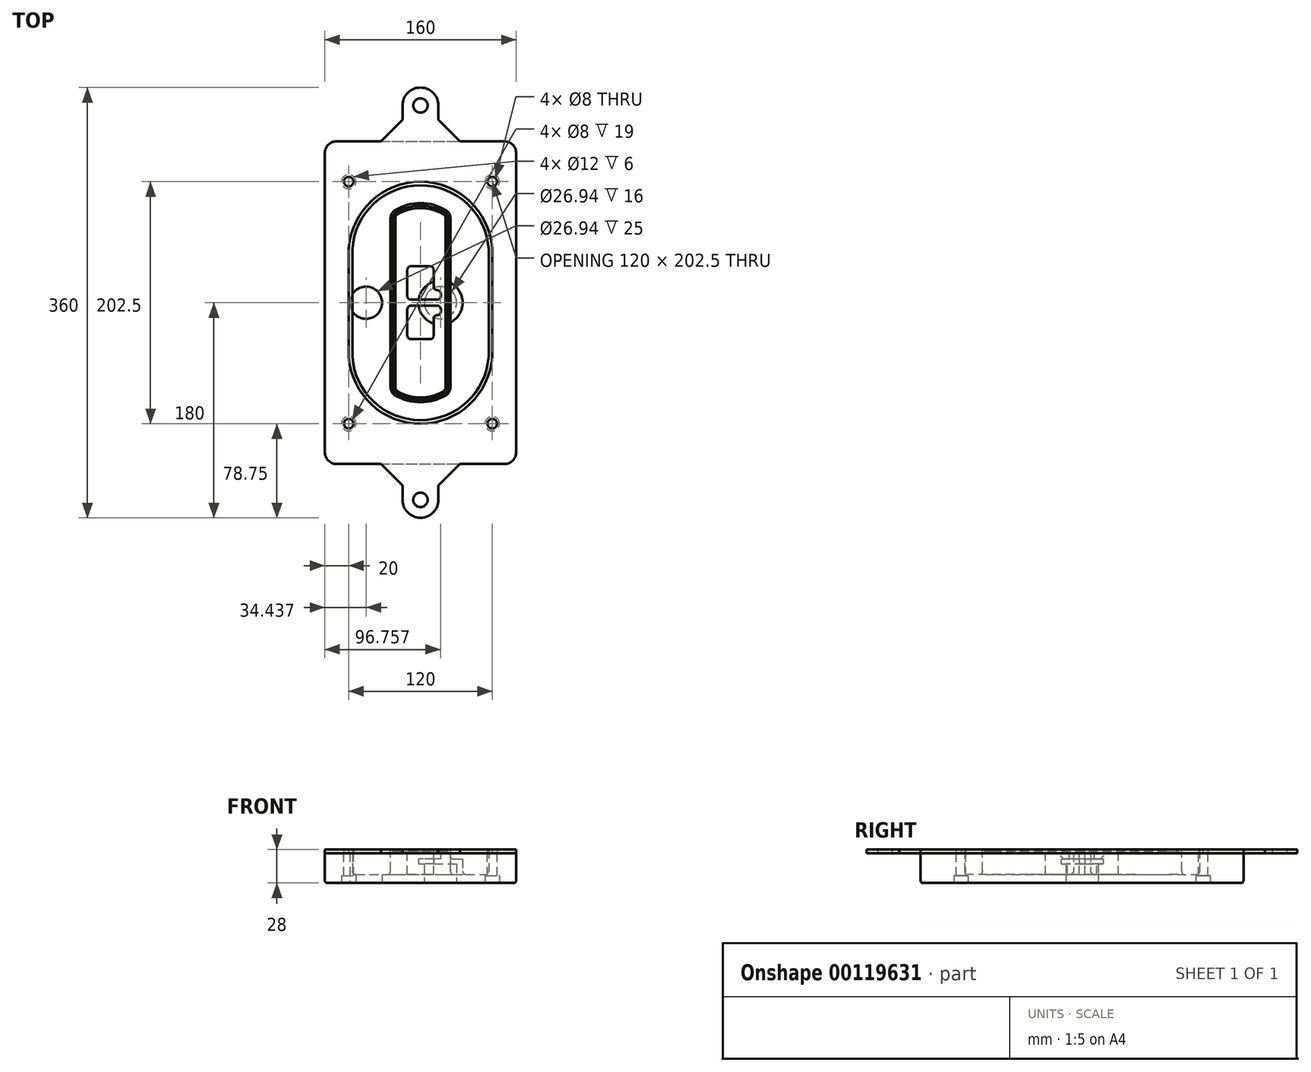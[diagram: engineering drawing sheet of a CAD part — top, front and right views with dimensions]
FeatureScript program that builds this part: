
annotation { "Feature Type Name" : "Feature", "Feature Type Description" : "" }
export const myFeature = defineFeature(function(context is Context, id is Id, definition is map)
    precondition{}
    {
        {
            var Q0;
            Q0=qCreatedBy(makeId("Top.planeOp"),FACE);
            var sketch = newSketch(context, id + "F0", { "sketchPlane" : qUnion([Q0])});
            skPoint(sketch, "E0.rect.middle", {"position": v(0, 0) * mm});
            skLineSegment(sketch, "E1.bottom", {"start": v(-70, -135) * mm, "end": v(70, -135) * mm});
            skLineSegment(sketch, "E1.top", {"start": v(-70, 135) * mm, "end": v(70, 135) * mm});
            skLineSegment(sketch, "E1.left", {"start": v(-80, -125) * mm, "end": v(-80, 125) * mm});
            skLineSegment(sketch, "E1.right", {"start": v(80, -125) * mm, "end": v(80, 125) * mm});
            skLineSegment(sketch, "E2", {"start": v(-80, 135) * mm, "end": v(80, -135) * mm, "construction": true});
            skLineSegment(sketch, "E3", {"start": v(80, 135) * mm, "end": v(-80, -135) * mm, "construction": true});
            skCircle(sketch, "E4", {"center": v(-60, 101.25) * mm, "radius": 4 * mm});
            skCircle(sketch, "E5", {"center": v(60, 101.25) * mm, "radius": 4 * mm});
            skCircle(sketch, "E6", {"center": v(60, -101.25) * mm, "radius": 4 * mm});
            skCircle(sketch, "E7", {"center": v(-60, -101.25) * mm, "radius": 4 * mm});
            skLineSegment(sketch, "E8", {"start": v(-60, 101.25) * mm, "end": v(60, 101.25) * mm, "construction": true});
            skLineSegment(sketch, "E9", {"start": v(60, 101.25) * mm, "end": v(60, -101.25) * mm, "construction": true});
            skLineSegment(sketch, "E10", {"start": v(60, -101.25) * mm, "end": v(-60, -101.25) * mm, "construction": true});
            skLineSegment(sketch, "E11", {"start": v(-60, -101.25) * mm, "end": v(-60, 101.25) * mm, "construction": true});
            skLineSegment(sketch, "E12", {"start": v(-60, 44.66) * mm, "end": v(-60, -44.66) * mm});
            skLineSegment(sketch, "E13", {"start": v(60, 44.66) * mm, "end": v(60, -44.66) * mm});
            skArc(sketch, "E14", {"start": v(59.98, 45.37) * mm, "mid": v(0, 101.25) * mm, "end": v(-59.98, 45.37) * mm});
            skArc(sketch, "E15", {"start": v(-59.98, -45.37) * mm, "mid": v(0, -101.25) * mm, "end": v(59.98, -45.37) * mm});
            skLineSegment(sketch, "E16", {"start": v(-60, 0) * mm, "end": v(60, 0) * mm, "construction": true});
            skPoint(sketch, "E17.visualSharp", {"position": v(-60, -45) * mm});
            skArc(sketch, "E17.filletArc", {"start": v(-60, -44.66) * mm, "mid": v(-60, -45.02) * mm, "end": v(-59.98, -45.37) * mm});
            skPoint(sketch, "E18.visualSharp", {"position": v(-60, 45) * mm});
            skArc(sketch, "E18.filletArc", {"start": v(-59.98, 45.37) * mm, "mid": v(-60, 45.02) * mm, "end": v(-60, 44.66) * mm});
            skPoint(sketch, "E19.visualSharp", {"position": v(60, 45) * mm});
            skArc(sketch, "E19.filletArc", {"start": v(60, 44.66) * mm, "mid": v(60, 45.02) * mm, "end": v(59.98, 45.37) * mm});
            skPoint(sketch, "E20.visualSharp", {"position": v(60, -45) * mm});
            skArc(sketch, "E20.filletArc", {"start": v(59.98, -45.37) * mm, "mid": v(60, -45.02) * mm, "end": v(60, -44.66) * mm});
            skPoint(sketch, "E21.visualSharp", {"position": v(-80, 135) * mm});
            skArc(sketch, "E21.filletArc", {"start": v(-70, 135) * mm, "mid": v(-77.07, 132.07) * mm, "end": v(-80, 125) * mm});
            skPoint(sketch, "E22.visualSharp", {"position": v(80, 135) * mm});
            skArc(sketch, "E22.filletArc", {"start": v(80, 125) * mm, "mid": v(77.07, 132.07) * mm, "end": v(70, 135) * mm});
            skPoint(sketch, "E23.visualSharp", {"position": v(80, -135) * mm});
            skArc(sketch, "E23.filletArc", {"start": v(70, -135) * mm, "mid": v(77.07, -132.07) * mm, "end": v(80, -125) * mm});
            skPoint(sketch, "E24.visualSharp", {"position": v(-80, -135) * mm});
            skArc(sketch, "E24.filletArc", {"start": v(-80, -125) * mm, "mid": v(-77.07, -132.07) * mm, "end": v(-70, -135) * mm});
            skArc(sketch, "E25.0", {"start": v(57, 44.66) * mm, "mid": v(57, 44.9) * mm, "end": v(56.98, 45.16) * mm});
            skLineSegment(sketch, "E25.1", {"start": v(57, 44.66) * mm, "end": v(57, -44.66) * mm});
            skArc(sketch, "E25.2", {"start": v(56.98, -45.16) * mm, "mid": v(57, -44.9) * mm, "end": v(57, -44.66) * mm});
            skArc(sketch, "E25.3", {"start": v(-56.98, -45.16) * mm, "mid": v(0, -98.25) * mm, "end": v(56.98, -45.16) * mm});
            skArc(sketch, "E25.4", {"start": v(-57, -44.66) * mm, "mid": v(-57, -44.9) * mm, "end": v(-56.98, -45.16) * mm});
            skArc(sketch, "E25.5", {"start": v(56.98, 45.16) * mm, "mid": v(0, 98.25) * mm, "end": v(-56.98, 45.16) * mm});
            skLineSegment(sketch, "E25.6", {"start": v(-57, 44.66) * mm, "end": v(-57, -44.66) * mm});
            skArc(sketch, "E25.7", {"start": v(-56.98, 45.16) * mm, "mid": v(-57, 44.9) * mm, "end": v(-57, 44.66) * mm});
            skArc(sketch, "E26.0", {"start": v(-63.97, 45.65) * mm, "mid": v(-64, 45.16) * mm, "end": v(-64, 44.66) * mm});
            skArc(sketch, "E26.1", {"start": v(63.97, 45.65) * mm, "mid": v(0, 105.25) * mm, "end": v(-63.97, 45.65) * mm});
            skArc(sketch, "E26.2", {"start": v(64, 44.66) * mm, "mid": v(64, 45.16) * mm, "end": v(63.97, 45.65) * mm});
            skLineSegment(sketch, "E26.3", {"start": v(64, 44.66) * mm, "end": v(64, -44.66) * mm});
            skArc(sketch, "E26.4", {"start": v(63.97, -45.65) * mm, "mid": v(64, -45.16) * mm, "end": v(64, -44.66) * mm});
            skLineSegment(sketch, "E26.5", {"start": v(-64, 44.66) * mm, "end": v(-64, -44.66) * mm});
            skArc(sketch, "E26.6", {"start": v(-63.97, -45.65) * mm, "mid": v(0, -105.25) * mm, "end": v(63.97, -45.65) * mm});
            skArc(sketch, "E26.7", {"start": v(-64, -44.66) * mm, "mid": v(-64, -45.16) * mm, "end": v(-63.97, -45.65) * mm});
            skSolve(sketch);
        }
        {
            var Q0;
            Q0=makeQuery(id+"F0.imprint","IMPRINT",FACE,{"disambiguationData":[TD([[makeQuery(id+"F0.imprint","IMPRINT",EDGE,{"derivedFrom":sQuery(id+"F0.wireOp",EDGE,"E1.bottom")}),1.0]])]});
            var Q1;
            Q1=makeQuery(id+"F0.imprint","IMPRINT",FACE,{"disambiguationData":[TD([[makeQuery(id+"F0.imprint","IMPRINT",EDGE,{"derivedFrom":sQuery(id+"F0.wireOp",EDGE,"E12")}),1.0]])]});
            var Q2;
            Q2=makeQuery(id+"F0.imprint","IMPRINT",FACE,{"disambiguationData":[TD([[makeQuery(id+"F0.imprint","IMPRINT",EDGE,{"derivedFrom":sQuery(id+"F0.wireOp",EDGE,"E25.0")}),1.0]])]});
            var Q3;
            Q3=makeQuery(id+"F0.imprint","IMPRINT",FACE,{"disambiguationData":[TD([[makeQuery(id+"F0.imprint","IMPRINT",EDGE,{"derivedFrom":sQuery(id+"F0.wireOp",EDGE,"E12")}),-1.0]])]});
            extrude(context, id + "F1", {"entities" : qUnion([Q0, Q1, Q2, Q3]), "oppositeDirection" : true, "depth" : 25 * mm});
        }
        {
            var Q0;
            Q0=makeQuery(id+"F0.imprint","IMPRINT",FACE,{"disambiguationData":[TD([[makeQuery(id+"F0.imprint","IMPRINT",EDGE,{"derivedFrom":sQuery(id+"F0.wireOp",EDGE,"E12")}),1.0]])]});
            extrude(context, id + "F2", {"entities" : qUnion([Q0]), "operationType" : NewBodyOperationType.ADD, "depth" : 3 * mm});
        }
        {
            var Q0;
            Q0=makeQuery(id+"F0.imprint","IMPRINT",FACE,{"disambiguationData":[TD([[makeQuery(id+"F0.imprint","IMPRINT",EDGE,{"derivedFrom":sQuery(id+"F0.wireOp",EDGE,"E25.0")}),1.0]])]});
            extrude(context, id + "F3", {"entities" : qUnion([Q0]), "operationType" : NewBodyOperationType.REMOVE, "oppositeDirection" : true, "depth" : 18 * mm});
        }
        {
            var Q0;
            Q0=makeQuery(id+"F2.opExtrude","CAP_FACE",FACE,{"disambiguationData":[OSD([sQuery(id+"F0.wireOp",EDGE,"E12"),sQuery(id+"F0.wireOp",EDGE,"E13"),sQuery(id+"F0.wireOp",EDGE,"E14"),sQuery(id+"F0.wireOp",EDGE,"E15"),sQuery(id+"F0.wireOp",EDGE,"E17.filletArc"),sQuery(id+"F0.wireOp",EDGE,"E18.filletArc"),sQuery(id+"F0.wireOp",EDGE,"E19.filletArc"),sQuery(id+"F0.wireOp",EDGE,"E20.filletArc"),sQuery(id+"F0.wireOp",EDGE,"E25.0"),sQuery(id+"F0.wireOp",EDGE,"E25.1"),sQuery(id+"F0.wireOp",EDGE,"E25.2"),sQuery(id+"F0.wireOp",EDGE,"E25.3"),sQuery(id+"F0.wireOp",EDGE,"E25.4"),sQuery(id+"F0.wireOp",EDGE,"E25.5"),sQuery(id+"F0.wireOp",EDGE,"E25.6"),sQuery(id+"F0.wireOp",EDGE,"E25.7")])],"isStart":false});
            var sketch = newSketch(context, id + "F4", { "sketchPlane" : qUnion([Q0])});
            skArc(sketch, "E27.0", {"start": v(-20.99, -77.65) * mm, "mid": v(0, -83.25) * mm, "end": v(20.99, -77.65) * mm});
            skArc(sketch, "E28.0", {"start": v(20.99, 77.65) * mm, "mid": v(0, 83.25) * mm, "end": v(-20.99, 77.65) * mm});
            skLineSegment(sketch, "E29", {"start": v(-25, 70.71) * mm, "end": v(-25, -70.71) * mm});
            skLineSegment(sketch, "E30", {"start": v(25, 70.71) * mm, "end": v(25, -70.71) * mm});
            skLineSegment(sketch, "E31", {"start": v(-25, 75.03) * mm, "end": v(25, 75.03) * mm, "construction": true});
            skLineSegment(sketch, "E32", {"start": v(-25, -75.03) * mm, "end": v(25, -75.03) * mm, "construction": true});
            skPoint(sketch, "E33.visualSharp", {"position": v(-25, 75.03) * mm});
            skArc(sketch, "E33.filletArc", {"start": v(-20.99, 77.65) * mm, "mid": v(-23.92, 74.72) * mm, "end": v(-25, 70.71) * mm});
            skPoint(sketch, "E34.visualSharp", {"position": v(25, 75.03) * mm});
            skArc(sketch, "E34.filletArc", {"start": v(25, 70.71) * mm, "mid": v(23.92, 74.72) * mm, "end": v(20.99, 77.65) * mm});
            skPoint(sketch, "E35.visualSharp", {"position": v(25, -75.03) * mm});
            skArc(sketch, "E35.filletArc", {"start": v(20.99, -77.65) * mm, "mid": v(23.92, -74.72) * mm, "end": v(25, -70.71) * mm});
            skPoint(sketch, "E36.visualSharp", {"position": v(-25, -75.03) * mm});
            skArc(sketch, "E36.filletArc", {"start": v(-25, -70.71) * mm, "mid": v(-23.92, -74.72) * mm, "end": v(-20.99, -77.65) * mm});
            skArc(sketch, "E37.0", {"start": v(56.98, 45.16) * mm, "mid": v(0, 98.25) * mm, "end": v(-56.98, 45.16) * mm});
            skArc(sketch, "E37.1", {"start": v(-56.98, 45.16) * mm, "mid": v(-57, 44.9) * mm, "end": v(-57, 44.66) * mm});
            skLineSegment(sketch, "E37.2", {"start": v(-57, 44.66) * mm, "end": v(-57, -44.66) * mm});
            skArc(sketch, "E37.3", {"start": v(-57, -44.66) * mm, "mid": v(-57, -44.9) * mm, "end": v(-56.98, -45.16) * mm});
            skArc(sketch, "E37.4", {"start": v(-56.98, -45.16) * mm, "mid": v(0, -98.25) * mm, "end": v(56.98, -45.16) * mm});
            skArc(sketch, "E37.5", {"start": v(56.98, -45.16) * mm, "mid": v(57, -44.9) * mm, "end": v(57, -44.66) * mm});
            skLineSegment(sketch, "E37.6", {"start": v(57, 44.66) * mm, "end": v(57, -44.66) * mm});
            skArc(sketch, "E37.7", {"start": v(57, 44.66) * mm, "mid": v(57, 44.9) * mm, "end": v(56.98, 45.16) * mm});
            skLineSegment(sketch, "E38.0", {"start": v(23, 70.71) * mm, "end": v(23, -70.71) * mm});
            skArc(sketch, "E38.1", {"start": v(19.99, -75.92) * mm, "mid": v(22.2, -73.72) * mm, "end": v(23, -70.71) * mm});
            skArc(sketch, "E38.2", {"start": v(-19.99, -75.92) * mm, "mid": v(0, -81.25) * mm, "end": v(19.99, -75.92) * mm});
            skArc(sketch, "E38.3", {"start": v(-23, -70.71) * mm, "mid": v(-22.2, -73.72) * mm, "end": v(-19.99, -75.92) * mm});
            skLineSegment(sketch, "E38.4", {"start": v(-23, 70.71) * mm, "end": v(-23, -70.71) * mm});
            skArc(sketch, "E38.5", {"start": v(23, 70.71) * mm, "mid": v(22.2, 73.72) * mm, "end": v(19.99, 75.92) * mm});
            skArc(sketch, "E38.6", {"start": v(-19.99, 75.92) * mm, "mid": v(-22.2, 73.72) * mm, "end": v(-23, 70.71) * mm});
            skArc(sketch, "E38.7", {"start": v(19.99, 75.92) * mm, "mid": v(0, 81.25) * mm, "end": v(-19.99, 75.92) * mm});
            skArc(sketch, "E39.0", {"start": v(21, 70.71) * mm, "mid": v(20.46, 72.72) * mm, "end": v(19, 74.18) * mm});
            skLineSegment(sketch, "E39.1", {"start": v(21, 70.71) * mm, "end": v(21, -70.71) * mm});
            skArc(sketch, "E39.2", {"start": v(19, -74.18) * mm, "mid": v(20.46, -72.72) * mm, "end": v(21, -70.71) * mm});
            skArc(sketch, "E39.3", {"start": v(-19, -74.18) * mm, "mid": v(0, -79.25) * mm, "end": v(19, -74.18) * mm});
            skArc(sketch, "E39.4", {"start": v(-21, -70.71) * mm, "mid": v(-20.46, -72.72) * mm, "end": v(-19, -74.18) * mm});
            skArc(sketch, "E39.5", {"start": v(19, 74.18) * mm, "mid": v(0, 79.25) * mm, "end": v(-19, 74.18) * mm});
            skLineSegment(sketch, "E39.6", {"start": v(-21, 70.71) * mm, "end": v(-21, -70.71) * mm});
            skArc(sketch, "E39.7", {"start": v(-19, 74.18) * mm, "mid": v(-20.46, 72.72) * mm, "end": v(-21, 70.71) * mm});
            skLineSegment(sketch, "E40", {"start": v(-25, 0) * mm, "end": v(25, 0) * mm, "construction": true});
            skLineSegment(sketch, "E41", {"start": v(-11, 5.5) * mm, "end": v(-11, 27.5) * mm});
            skLineSegment(sketch, "E42", {"start": v(-8, 30.5) * mm, "end": v(8, 30.5) * mm});
            skLineSegment(sketch, "E43", {"start": v(11, 27.5) * mm, "end": v(11, 13.5) * mm});
            skLineSegment(sketch, "E44", {"start": v(14, 10.5) * mm, "end": v(14, 10.5) * mm});
            skLineSegment(sketch, "E45", {"start": v(17, 7.5) * mm, "end": v(17, 5.5) * mm});
            skLineSegment(sketch, "E46", {"start": v(14, 2.5) * mm, "end": v(-8, 2.5) * mm});
            skPoint(sketch, "E47.visualSharp", {"position": v(-11, 30.5) * mm});
            skArc(sketch, "E47.filletArc", {"start": v(-8, 30.5) * mm, "mid": v(-10.12, 29.62) * mm, "end": v(-11, 27.5) * mm});
            skPoint(sketch, "E48.visualSharp", {"position": v(11, 30.5) * mm});
            skArc(sketch, "E48.filletArc", {"start": v(11, 27.5) * mm, "mid": v(10.12, 29.62) * mm, "end": v(8, 30.5) * mm});
            skPoint(sketch, "E49.visualSharp", {"position": v(11, 10.5) * mm});
            skArc(sketch, "E49.filletArc", {"start": v(11, 13.5) * mm, "mid": v(11.88, 11.38) * mm, "end": v(14, 10.5) * mm});
            skPoint(sketch, "E50.visualSharp", {"position": v(17, 10.5) * mm});
            skArc(sketch, "E50.filletArc", {"start": v(17, 7.5) * mm, "mid": v(16.12, 9.62) * mm, "end": v(14, 10.5) * mm});
            skPoint(sketch, "E51.visualSharp", {"position": v(17, 2.5) * mm});
            skArc(sketch, "E51.filletArc", {"start": v(14, 2.5) * mm, "mid": v(16.12, 3.38) * mm, "end": v(17, 5.5) * mm});
            skPoint(sketch, "E52.visualSharp", {"position": v(-11, 2.5) * mm});
            skArc(sketch, "E52.filletArc", {"start": v(-11, 5.5) * mm, "mid": v(-10.12, 3.38) * mm, "end": v(-8, 2.5) * mm});
            skLineSegment(sketch, "E53.0.MirrorCS", {"start": v(14, -2.5) * mm, "end": v(-8, -2.5) * mm});
            skArc(sketch, "E54.0.MirrorCS", {"start": v(-11, -5.5) * mm, "mid": v(-10.12, -3.38) * mm, "end": v(-8, -2.5) * mm});
            skLineSegment(sketch, "E55.0.MirrorCS", {"start": v(-11, -5.5) * mm, "end": v(-11, -27.5) * mm});
            skArc(sketch, "E56.0.MirrorCS", {"start": v(-8, -30.5) * mm, "mid": v(-10.12, -29.62) * mm, "end": v(-11, -27.5) * mm});
            skLineSegment(sketch, "E57.0.MirrorCS", {"start": v(-8, -30.5) * mm, "end": v(8, -30.5) * mm});
            skArc(sketch, "E58.0.MirrorCS", {"start": v(11, -27.5) * mm, "mid": v(10.12, -29.62) * mm, "end": v(8, -30.5) * mm});
            skLineSegment(sketch, "E59.0.MirrorCS", {"start": v(11, -27.5) * mm, "end": v(11, -13.5) * mm});
            skArc(sketch, "E60.0.MirrorCS", {"start": v(11, -13.5) * mm, "mid": v(11.88, -11.38) * mm, "end": v(14, -10.5) * mm});
            skArc(sketch, "E61.0.MirrorCS", {"start": v(17, -7.5) * mm, "mid": v(16.12, -9.62) * mm, "end": v(14, -10.5) * mm});
            skLineSegment(sketch, "E62.0.MirrorCS", {"start": v(17, -7.5) * mm, "end": v(17, -5.5) * mm});
            skArc(sketch, "E63.0.MirrorCS", {"start": v(14, -2.5) * mm, "mid": v(16.12, -3.38) * mm, "end": v(17, -5.5) * mm});
            skSolve(sketch);
        }
        {
            var Q0;
            Q0=makeQuery(id+"F4.imprint","IMPRINT",FACE,{"disambiguationData":[TD([[makeQuery(id+"F4.imprint","IMPRINT",EDGE,{"derivedFrom":sQuery(id+"F4.wireOp",EDGE,"E27.0")}),1.0]])]});
            var Q1;
            Q1=makeQuery(id+"F4.imprint","IMPRINT",FACE,{"disambiguationData":[TD([[makeQuery(id+"F4.imprint","IMPRINT",EDGE,{"derivedFrom":sQuery(id+"F4.wireOp",EDGE,"E38.0")}),-1.0]])]});
            var Q2;
            Q2=makeQuery(id+"F4.imprint","IMPRINT",FACE,{"disambiguationData":[TD([[makeQuery(id+"F4.imprint","IMPRINT",EDGE,{"derivedFrom":sQuery(id+"F4.wireOp",EDGE,"E39.0")}),1.0]])]});
            extrude(context, id + "F5", {"entities" : qUnion([Q0, Q1, Q2]), "operationType" : NewBodyOperationType.ADD, "endBound" : BoundingType.UP_TO_NEXT, "oppositeDirection" : true, "depth" : 25 * mm});
        }
        {
            var Q0;
            Q0=makeQuery(id+"F4.imprint","IMPRINT",FACE,{"disambiguationData":[TD([[makeQuery(id+"F4.imprint","IMPRINT",EDGE,{"derivedFrom":sQuery(id+"F4.wireOp",EDGE,"E38.0")}),-1.0]])]});
            extrude(context, id + "F6", {"entities" : qUnion([Q0]), "operationType" : NewBodyOperationType.REMOVE, "oppositeDirection" : true, "depth" : 2 * mm});
        }
        {
            var Q0;
            Q0=makeQuery(id+"F1.opExtrude","CAP_FACE",FACE,{"disambiguationData":[OSD([sQuery(id+"F0.wireOp",EDGE,"E1.bottom"),sQuery(id+"F0.wireOp",EDGE,"E1.top"),sQuery(id+"F0.wireOp",EDGE,"E1.left"),sQuery(id+"F0.wireOp",EDGE,"E1.right"),sQuery(id+"F0.wireOp",EDGE,"E4"),sQuery(id+"F0.wireOp",EDGE,"E5"),sQuery(id+"F0.wireOp",EDGE,"E6"),sQuery(id+"F0.wireOp",EDGE,"E7"),sQuery(id+"F0.wireOp",EDGE,"E21.filletArc"),sQuery(id+"F0.wireOp",EDGE,"E22.filletArc"),sQuery(id+"F0.wireOp",EDGE,"E23.filletArc"),sQuery(id+"F0.wireOp",EDGE,"E24.filletArc")])],"isStart":false});
            var sketch = newSketch(context, id + "F7", { "sketchPlane" : qUnion([Q0])});
            skCircle(sketch, "E64", {"center": v(16.76, 0) * mm, "radius": 13.47 * mm});
            skCircle(sketch, "E65", {"center": v(-45.56, 0) * mm, "radius": 13.47 * mm});
            skLineSegment(sketch, "E66", {"start": v(80, 0) * mm, "end": v(-80, 0) * mm});
            skCircle(sketch, "E67", {"center": v(16.76, 0) * mm, "radius": 18.47 * mm});
            skCircle(sketch, "E68", {"center": v(60, -101.25) * mm, "radius": 6 * mm});
            skCircle(sketch, "E69", {"center": v(-60, -101.25) * mm, "radius": 6 * mm});
            skCircle(sketch, "E70", {"center": v(-60, 101.25) * mm, "radius": 6 * mm});
            skCircle(sketch, "E71", {"center": v(60, 101.25) * mm, "radius": 6 * mm});
            skSolve(sketch);
        }
        {
            var Q0;
            {var subQ1=sQuery(id+"F7.wireOp",EDGE,"E66");var subQ4=sQuery(id+"F7.wireOp",EDGE,"E64");var subQ6=makeQuery(id+"F7.imprint","INTERSECT",VERTEX,{"disambiguationData":[OD(0.0)],"derivedFrom":[subQ4,subQ1]});Q0=makeQuery(id+"F7.imprint","IMPRINT",FACE,{"disambiguationData":[TD([[makeQuery(id+"F7.imprint","IMPRINT",EDGE,{"disambiguationData":[TD([[subQ6,-1.0]])],"derivedFrom":subQ4}),-1.0]])]});}
            var Q1;
            {var subQ0=sQuery(id+"F7.wireOp",EDGE,"E66");var subQ1=sQuery(id+"F7.wireOp",EDGE,"E64");var subQ3=makeQuery(id+"F7.imprint","INTERSECT",VERTEX,{"disambiguationData":[OD(0.0)],"derivedFrom":[subQ1,subQ0]});Q1=makeQuery(id+"F7.imprint","IMPRINT",FACE,{"disambiguationData":[TD([[makeQuery(id+"F7.imprint","IMPRINT",EDGE,{"disambiguationData":[TD([[subQ3,-1.0]])],"derivedFrom":subQ1}),1.0]])]});}
            var Q2;
            {var subQ0=sQuery(id+"F7.wireOp",EDGE,"E66");var subQ1=sQuery(id+"F7.wireOp",EDGE,"E64");var subQ3=makeQuery(id+"F7.imprint","INTERSECT",VERTEX,{"disambiguationData":[OD(0.0)],"derivedFrom":[subQ1,subQ0]});Q2=makeQuery(id+"F7.imprint","IMPRINT",FACE,{"disambiguationData":[TD([[makeQuery(id+"F7.imprint","IMPRINT",EDGE,{"disambiguationData":[TD([[subQ3,1.0]])],"derivedFrom":subQ1}),1.0]])]});}
            var Q3;
            {var subQ1=sQuery(id+"F7.wireOp",EDGE,"E66");var subQ4=sQuery(id+"F7.wireOp",EDGE,"E64");var subQ6=makeQuery(id+"F7.imprint","INTERSECT",VERTEX,{"disambiguationData":[OD(0.0)],"derivedFrom":[subQ4,subQ1]});Q3=makeQuery(id+"F7.imprint","IMPRINT",FACE,{"disambiguationData":[TD([[makeQuery(id+"F7.imprint","IMPRINT",EDGE,{"disambiguationData":[TD([[subQ6,1.0]])],"derivedFrom":subQ4}),-1.0]])]});}
            extrude(context, id + "F8", {"entities" : qUnion([Q0, Q1, Q2, Q3]), "operationType" : NewBodyOperationType.ADD, "oppositeDirection" : true, "depth" : 20 * mm});
        }
        {
            var Q0;
            {var subQ0=sQuery(id+"F7.wireOp",EDGE,"E66");var subQ1=sQuery(id+"F7.wireOp",EDGE,"E64");var subQ3=makeQuery(id+"F7.imprint","INTERSECT",VERTEX,{"disambiguationData":[OD(0.0)],"derivedFrom":[subQ1,subQ0]});Q0=makeQuery(id+"F7.imprint","IMPRINT",FACE,{"disambiguationData":[TD([[makeQuery(id+"F7.imprint","IMPRINT",EDGE,{"disambiguationData":[TD([[subQ3,-1.0]])],"derivedFrom":subQ1}),1.0]])]});}
            var Q1;
            {var subQ0=sQuery(id+"F7.wireOp",EDGE,"E66");var subQ1=sQuery(id+"F7.wireOp",EDGE,"E64");var subQ3=makeQuery(id+"F7.imprint","INTERSECT",VERTEX,{"disambiguationData":[OD(0.0)],"derivedFrom":[subQ1,subQ0]});Q1=makeQuery(id+"F7.imprint","IMPRINT",FACE,{"disambiguationData":[TD([[makeQuery(id+"F7.imprint","IMPRINT",EDGE,{"disambiguationData":[TD([[subQ3,1.0]])],"derivedFrom":subQ1}),1.0]])]});}
            extrude(context, id + "F9", {"entities" : qUnion([Q0, Q1]), "operationType" : NewBodyOperationType.REMOVE, "oppositeDirection" : true, "depth" : 16 * mm});
        }
        {
            var Q0;
            {var subQ0=sQuery(id+"F7.wireOp",EDGE,"E66");var subQ1=sQuery(id+"F7.wireOp",EDGE,"E65");var subQ3=makeQuery(id+"F7.imprint","INTERSECT",VERTEX,{"disambiguationData":[OD(0.0)],"derivedFrom":[subQ1,subQ0]});Q0=makeQuery(id+"F7.imprint","IMPRINT",FACE,{"disambiguationData":[TD([[makeQuery(id+"F7.imprint","IMPRINT",EDGE,{"disambiguationData":[TD([[subQ3,-1.0]])],"derivedFrom":subQ1}),1.0]])]});}
            var Q1;
            {var subQ0=sQuery(id+"F7.wireOp",EDGE,"E66");var subQ1=sQuery(id+"F7.wireOp",EDGE,"E65");var subQ3=makeQuery(id+"F7.imprint","INTERSECT",VERTEX,{"disambiguationData":[OD(0.0)],"derivedFrom":[subQ1,subQ0]});Q1=makeQuery(id+"F7.imprint","IMPRINT",FACE,{"disambiguationData":[TD([[makeQuery(id+"F7.imprint","IMPRINT",EDGE,{"disambiguationData":[TD([[subQ3,1.0]])],"derivedFrom":subQ1}),1.0]])]});}
            extrude(context, id + "F10", {"entities" : qUnion([Q0, Q1]), "operationType" : NewBodyOperationType.REMOVE, "oppositeDirection" : true, "depth" : 25 * mm});
        }
        {
            var Q0;
            Q0=makeQuery(id+"F7.imprint","IMPRINT",FACE,{"disambiguationData":[TD([[makeQuery(id+"F7.imprint","IMPRINT",EDGE,{"derivedFrom":sQuery(id+"F7.wireOp",EDGE,"E68")}),1.0]])]});
            var Q1;
            Q1=makeQuery(id+"F7.imprint","IMPRINT",FACE,{"disambiguationData":[TD([[makeQuery(id+"F7.imprint","IMPRINT",EDGE,{"derivedFrom":makeQuery(id+"F1.opExtrude","CAP_EDGE",EDGE,{"disambiguationData":[OSD([sQuery(id+"F0.wireOp",EDGE,"E5")])],"isStart":false})}),-1.0]])]});
            var Q2;
            Q2=makeQuery(id+"F7.imprint","IMPRINT",FACE,{"disambiguationData":[TD([[makeQuery(id+"F7.imprint","IMPRINT",EDGE,{"derivedFrom":sQuery(id+"F7.wireOp",EDGE,"E69")}),1.0]])]});
            var Q3;
            Q3=makeQuery(id+"F7.imprint","IMPRINT",FACE,{"disambiguationData":[TD([[makeQuery(id+"F7.imprint","IMPRINT",EDGE,{"derivedFrom":makeQuery(id+"F1.opExtrude","CAP_EDGE",EDGE,{"disambiguationData":[OSD([sQuery(id+"F0.wireOp",EDGE,"E4")])],"isStart":false})}),-1.0]])]});
            var Q4;
            Q4=makeQuery(id+"F7.imprint","IMPRINT",FACE,{"disambiguationData":[TD([[makeQuery(id+"F7.imprint","IMPRINT",EDGE,{"derivedFrom":sQuery(id+"F7.wireOp",EDGE,"E70")}),1.0]])]});
            var Q5;
            Q5=makeQuery(id+"F7.imprint","IMPRINT",FACE,{"disambiguationData":[TD([[makeQuery(id+"F7.imprint","IMPRINT",EDGE,{"derivedFrom":makeQuery(id+"F1.opExtrude","CAP_EDGE",EDGE,{"disambiguationData":[OSD([sQuery(id+"F0.wireOp",EDGE,"E7")])],"isStart":false})}),-1.0]])]});
            var Q6;
            Q6=makeQuery(id+"F7.imprint","IMPRINT",FACE,{"disambiguationData":[TD([[makeQuery(id+"F7.imprint","IMPRINT",EDGE,{"derivedFrom":sQuery(id+"F7.wireOp",EDGE,"E71")}),1.0]])]});
            var Q7;
            Q7=makeQuery(id+"F7.imprint","IMPRINT",FACE,{"disambiguationData":[TD([[makeQuery(id+"F7.imprint","IMPRINT",EDGE,{"derivedFrom":makeQuery(id+"F1.opExtrude","CAP_EDGE",EDGE,{"disambiguationData":[OSD([sQuery(id+"F0.wireOp",EDGE,"E6")])],"isStart":false})}),-1.0]])]});
            extrude(context, id + "F11", {"entities" : qUnion([Q0, Q1, Q2, Q3, Q4, Q5, Q6, Q7]), "operationType" : NewBodyOperationType.REMOVE, "oppositeDirection" : true, "depth" : 6 * mm});
        }
        {
            var Q0;
            Q0=makeQuery(id+"F9.boolean.opBoolean","COPY",FACE,{"derivedFrom":makeQuery(id+"F9.opExtrude","CAP_FACE",FACE,{"disambiguationData":[OSD([sQuery(id+"F7.wireOp",EDGE,"E64")])],"isStart":false})});
            var sketch = newSketch(context, id + "F12", { "sketchPlane" : qUnion([Q0])});
            skArc(sketch, "E72.0", {"start": v(11, 17.55) * mm, "mid": v(2.57, 11.82) * mm, "end": v(-1.54, 2.5) * mm});
            skArc(sketch, "E72.1", {"start": v(-1.54, -2.5) * mm, "mid": v(2.57, -11.82) * mm, "end": v(11, -17.55) * mm});
            skLineSegment(sketch, "E73", {"start": v(-1.54, -2.5) * mm, "end": v(14, -2.5) * mm});
            skLineSegment(sketch, "E74.0", {"start": v(14, 2.5) * mm, "end": v(-1.54, 2.5) * mm});
            skArc(sketch, "E74.1", {"start": v(14, 2.5) * mm, "mid": v(16.12, 3.38) * mm, "end": v(17, 5.5) * mm});
            skLineSegment(sketch, "E74.2", {"start": v(17, 7.5) * mm, "end": v(17, 5.5) * mm});
            skArc(sketch, "E74.3", {"start": v(17, 7.5) * mm, "mid": v(16.12, 9.62) * mm, "end": v(14, 10.5) * mm});
            skArc(sketch, "E74.4", {"start": v(11, 13.5) * mm, "mid": v(11.88, 11.38) * mm, "end": v(14, 10.5) * mm});
            skLineSegment(sketch, "E74.5", {"start": v(11, 17.55) * mm, "end": v(11, 13.5) * mm});
            skLineSegment(sketch, "E74.7", {"start": v(14, -2.5) * mm, "end": v(-1.54, -2.5) * mm});
            skArc(sketch, "E74.8", {"start": v(14, -2.5) * mm, "mid": v(16.12, -3.38) * mm, "end": v(17, -5.5) * mm});
            skLineSegment(sketch, "E74.9", {"start": v(17, -7.5) * mm, "end": v(17, -5.5) * mm});
            skArc(sketch, "E74.10", {"start": v(17, -7.5) * mm, "mid": v(16.12, -9.62) * mm, "end": v(14, -10.5) * mm});
            skArc(sketch, "E74.11", {"start": v(11, -13.5) * mm, "mid": v(11.88, -11.38) * mm, "end": v(14, -10.5) * mm});
            skLineSegment(sketch, "E74.12", {"start": v(11, -17.55) * mm, "end": v(11, -13.5) * mm});
            skPoint(sketch, "E75.orphan", {"position": v(11, -27.5) * mm});
            skPoint(sketch, "E76.orphan", {"position": v(-8, -2.5) * mm});
            skPoint(sketch, "E77.orphan", {"position": v(-8, 2.5) * mm});
            skPoint(sketch, "E78.orphan", {"position": v(11, 27.5) * mm});
            skSolve(sketch);
        }
        {
            var Q0;
            {var subQ7=sQuery(id+"F12.wireOp",EDGE,"E72.0");var subQ14=sQuery(id+"F12.wireOp",EDGE,"E72.1");var subQ16=sQuery(id+"F12.wireOp",EDGE,"E74.1");var subQ18=sQuery(id+"F12.wireOp",EDGE,"E74.8");Q0=qUnion([makeQuery(id+"F12.imprint","IMPRINT",FACE,{"disambiguationData":[TD([[makeQuery(id+"F12.imprint","IMPRINT",EDGE,{"derivedFrom":subQ7}),1.0]])]}),makeQuery(id+"F12.imprint","IMPRINT",FACE,{"disambiguationData":[TD([[makeQuery(id+"F12.imprint","IMPRINT",EDGE,{"derivedFrom":subQ14}),1.0]])]}),makeQuery(id+"F12.imprint","IMPRINT",FACE,{"disambiguationData":[TD([[makeQuery(id+"F12.imprint","IMPRINT",EDGE,{"derivedFrom":subQ16}),1.0]])]}),makeQuery(id+"F12.imprint","IMPRINT",FACE,{"disambiguationData":[TD([[makeQuery(id+"F12.imprint","IMPRINT",EDGE,{"derivedFrom":subQ18}),-1.0]])]})]);}
            var Q1;
            Q1=makeQuery(id+"F5.boolean.opBoolean","SPLIT",FACE,{"disambiguationData":[TD([makeQuery(id+"F5.opExtrude","SWEPT_FACE",FACE,{"disambiguationData":[OSD([sQuery(id+"F4.wireOp",EDGE,"E41")])]})])],"derivedFrom":makeQuery(id+"F3.boolean.opBoolean","COPY",FACE,{"derivedFrom":makeQuery(id+"F3.opExtrude","CAP_FACE",FACE,{"disambiguationData":[OSD([sQuery(id+"F0.wireOp",EDGE,"E25.0"),sQuery(id+"F0.wireOp",EDGE,"E25.1"),sQuery(id+"F0.wireOp",EDGE,"E25.2"),sQuery(id+"F0.wireOp",EDGE,"E25.3"),sQuery(id+"F0.wireOp",EDGE,"E25.4"),sQuery(id+"F0.wireOp",EDGE,"E25.5"),sQuery(id+"F0.wireOp",EDGE,"E25.6"),sQuery(id+"F0.wireOp",EDGE,"E25.7")])],"isStart":false})})});
            extrude(context, id + "F13", {"entities" : qUnion([Q0]), "operationType" : NewBodyOperationType.REMOVE, "endBound" : BoundingType.UP_TO_SURFACE, "endBoundEntityFace" : qUnion([Q1]), "depth" : 25 * mm});
        }
        {
            var Q0;
            Q0=makeQuery(id+"F3.boolean.opBoolean","COPY",EDGE,{"derivedFrom":makeQuery(id+"F3.opExtrude","CAP_EDGE",EDGE,{"disambiguationData":[OSD([sQuery(id+"F0.wireOp",EDGE,"E25.6")])],"isStart":false})});
            var Q1;
            Q1=makeQuery(id+"F8.boolean.opBoolean","INTERSECT",EDGE,{"derivedFrom":[makeQuery(id+"F5.opExtrude","SWEPT_FACE",FACE,{"disambiguationData":[OSD([sQuery(id+"F4.wireOp",EDGE,"E30")])]}),makeQuery(id+"F8.opExtrude","CAP_FACE",FACE,{"disambiguationData":[OSD([sQuery(id+"F7.wireOp",EDGE,"E67")])],"isStart":false})]});
            var Q2;
            Q2=makeQuery(id+"F8.boolean.opBoolean","INTERSECT",EDGE,{"disambiguationData":[OD(1.0)],"derivedFrom":[makeQuery(id+"F5.opExtrude","SWEPT_FACE",FACE,{"disambiguationData":[OSD([sQuery(id+"F4.wireOp",EDGE,"E30")])]}),makeQuery(id+"F8.opExtrude","SWEPT_FACE",FACE,{"disambiguationData":[OSD([sQuery(id+"F7.wireOp",EDGE,"E67")])]})]});
            var Q3;
            {var subQ0=sQuery(id+"F4.wireOp",EDGE,"E30");Q3=makeQuery(id+"F8.boolean.opBoolean","SPLIT",EDGE,{"disambiguationData":[TD([makeQuery(id+"F5.opExtrude","SWEPT_FACE",FACE,{"disambiguationData":[OSD([sQuery(id+"F4.wireOp",EDGE,"E35.filletArc")])]})])],"derivedFrom":makeQuery(id+"F5.opExtrude","CAP_EDGE",EDGE,{"disambiguationData":[OSD([subQ0])],"isStart":false})});}
            var Q4;
            {var subQ0=sQuery(id+"F0.wireOp",EDGE,"E25.7");var subQ1=sQuery(id+"F0.wireOp",EDGE,"E25.1");var subQ2=sQuery(id+"F0.wireOp",EDGE,"E25.6");var subQ3=sQuery(id+"F0.wireOp",EDGE,"E25.5");var subQ4=sQuery(id+"F0.wireOp",EDGE,"E25.4");var subQ5=sQuery(id+"F0.wireOp",EDGE,"E25.0");var subQ6=sQuery(id+"F0.wireOp",EDGE,"E25.2");var subQ7=sQuery(id+"F0.wireOp",EDGE,"E25.3");Q4=makeQuery(id+"F8.boolean.opBoolean","INTERSECT",EDGE,{"derivedFrom":[makeQuery(id+"F5.boolean.opBoolean","SPLIT",FACE,{"disambiguationData":[TD([makeQuery(id+"F2.opExtrude","SWEPT_FACE",FACE,{"disambiguationData":[OSD([subQ5])]})])],"derivedFrom":makeQuery(id+"F3.boolean.opBoolean","COPY",FACE,{"derivedFrom":makeQuery(id+"F3.opExtrude","CAP_FACE",FACE,{"disambiguationData":[OSD([subQ5,subQ1,subQ6,subQ7,subQ4,subQ3,subQ2,subQ0])],"isStart":false})})}),makeQuery(id+"F8.opExtrude","SWEPT_FACE",FACE,{"disambiguationData":[OSD([sQuery(id+"F7.wireOp",EDGE,"E67")])]})]});}
            var Q5;
            Q5=makeQuery(id+"F8.boolean.opBoolean","INTERSECT",EDGE,{"disambiguationData":[OD(0.0)],"derivedFrom":[makeQuery(id+"F5.opExtrude","SWEPT_FACE",FACE,{"disambiguationData":[OSD([sQuery(id+"F4.wireOp",EDGE,"E30")])]}),makeQuery(id+"F8.opExtrude","SWEPT_FACE",FACE,{"disambiguationData":[OSD([sQuery(id+"F7.wireOp",EDGE,"E67")])]})]});
            fillet(context, id + "F14", {"entities" : qUnion([Q0, Q1, Q2, Q3, Q4, Q5]), "radius" : 3 * mm, "tangentPropagation" : true, "allowEdgeOverflow" : false});
        }
        {
            var Q0;
            Q0=makeQuery(id+"F1.opExtrude","CAP_EDGE",EDGE,{"disambiguationData":[OSD([sQuery(id+"F0.wireOp",EDGE,"E1.bottom")])],"isStart":false});
            fillet(context, id + "F15", {"entities" : qUnion([Q0]), "radius" : 2 * mm, "tangentPropagation" : true, "allowEdgeOverflow" : false});
        }
        {
            var Q0;
            {var subQ0=sQuery(id+"F0.wireOp",EDGE,"E22.filletArc");var subQ1=sQuery(id+"F0.wireOp",EDGE,"E7");var subQ2=sQuery(id+"F0.wireOp",EDGE,"E6");var subQ3=sQuery(id+"F0.wireOp",EDGE,"E5");var subQ4=sQuery(id+"F0.wireOp",EDGE,"E4");var subQ5=sQuery(id+"F0.wireOp",EDGE,"E1.bottom");var subQ6=sQuery(id+"F0.wireOp",EDGE,"E21.filletArc");var subQ7=sQuery(id+"F0.wireOp",EDGE,"E1.top");var subQ8=sQuery(id+"F0.wireOp",EDGE,"E1.left");var subQ9=sQuery(id+"F0.wireOp",EDGE,"E1.right");var subQ10=sQuery(id+"F0.wireOp",EDGE,"E23.filletArc");var subQ11=sQuery(id+"F0.wireOp",EDGE,"E24.filletArc");Q0=makeQuery(id+"F2.boolean.opBoolean","SPLIT",FACE,{"disambiguationData":[TD([makeQuery(id+"F1.opExtrude","SWEPT_FACE",FACE,{"disambiguationData":[OSD([subQ5])]})])],"derivedFrom":makeQuery(id+"F1.opExtrude","CAP_FACE",FACE,{"disambiguationData":[OSD([subQ5,subQ7,subQ8,subQ9,subQ4,subQ3,subQ2,subQ1,subQ6,subQ0,subQ10,subQ11])],"isStart":true})});}
            var sketch = newSketch(context, id + "F16", { "sketchPlane" : qUnion([Q0])});
            skCircle(sketch, "E79", {"center": v(0, 165) * mm, "radius": 6 * mm});
            skLineSegment(sketch, "E80", {"start": v(0, 165) * mm, "end": v(0, 135) * mm, "construction": true});
            skArc(sketch, "E81", {"start": v(15, 165) * mm, "mid": v(0, 180) * mm, "end": v(-15, 165) * mm});
            skLineSegment(sketch, "E82", {"start": v(-15, 165) * mm, "end": v(-15, 153) * mm});
            skLineSegment(sketch, "E83", {"start": v(-15, 153) * mm, "end": v(-33, 135) * mm});
            skLineSegment(sketch, "E84", {"start": v(15, 165) * mm, "end": v(15, 153) * mm});
            skLineSegment(sketch, "E85", {"start": v(15, 153) * mm, "end": v(33, 135) * mm});
            skLineSegment(sketch, "E86", {"start": v(-80, 0) * mm, "end": v(80, 0) * mm, "construction": true});
            skLineSegment(sketch, "E87.MirrorCS", {"start": v(15, -153) * mm, "end": v(33, -135) * mm});
            skLineSegment(sketch, "E88.MirrorCS", {"start": v(15, -165) * mm, "end": v(15, -153) * mm});
            skLineSegment(sketch, "E89.MirrorCS", {"start": v(-15, -165) * mm, "end": v(-15, -153) * mm});
            skArc(sketch, "E90.MirrorCS", {"start": v(15, -165) * mm, "mid": v(0, -180) * mm, "end": v(-15, -165) * mm});
            skLineSegment(sketch, "E91.MirrorCS", {"start": v(0, -165) * mm, "end": v(0, -135) * mm, "construction": true});
            skCircle(sketch, "E92.MirrorC", {"center": v(0, -165) * mm, "radius": 6 * mm});
            skLineSegment(sketch, "E93.MirrorCS", {"start": v(-15, -153) * mm, "end": v(-33, -135) * mm});
            skSolve(sketch);
        }
        {
            var Q0;
            Q0=makeQuery(id+"F16.imprint","IMPRINT",FACE,{"disambiguationData":[TD([[makeQuery(id+"F16.imprint","IMPRINT",EDGE,{"derivedFrom":sQuery(id+"F16.wireOp",EDGE,"E79")}),-1.0]])]});
            var Q1;
            {var subQ0=sQuery(id+"F16.wireOp",EDGE,"E87.MirrorCS");Q1=makeQuery(id+"F16.imprint","IMPRINT",FACE,{"disambiguationData":[TD([[makeQuery(id+"F16.imprint","IMPRINT",EDGE,{"derivedFrom":subQ0}),1.0]])]});}
            var Q2;
            Q2=makeQuery(id+"F16.imprint","IMPRINT",FACE,{"disambiguationData":[TD([[makeQuery(id+"F16.imprint","IMPRINT",EDGE,{"derivedFrom":makeQuery(id+"F1.opExtrude","CAP_EDGE",EDGE,{"disambiguationData":[OSD([sQuery(id+"F0.wireOp",EDGE,"E1.left")])],"isStart":true})}),-1.0]])]});
            var Q3;
            Q3=makeQuery(id+"F2.opExtrude","CAP_FACE",FACE,{"disambiguationData":[OSD([sQuery(id+"F0.wireOp",EDGE,"E12"),sQuery(id+"F0.wireOp",EDGE,"E13"),sQuery(id+"F0.wireOp",EDGE,"E14"),sQuery(id+"F0.wireOp",EDGE,"E15"),sQuery(id+"F0.wireOp",EDGE,"E17.filletArc"),sQuery(id+"F0.wireOp",EDGE,"E18.filletArc"),sQuery(id+"F0.wireOp",EDGE,"E19.filletArc"),sQuery(id+"F0.wireOp",EDGE,"E20.filletArc"),sQuery(id+"F0.wireOp",EDGE,"E25.0"),sQuery(id+"F0.wireOp",EDGE,"E25.1"),sQuery(id+"F0.wireOp",EDGE,"E25.2"),sQuery(id+"F0.wireOp",EDGE,"E25.3"),sQuery(id+"F0.wireOp",EDGE,"E25.4"),sQuery(id+"F0.wireOp",EDGE,"E25.5"),sQuery(id+"F0.wireOp",EDGE,"E25.6"),sQuery(id+"F0.wireOp",EDGE,"E25.7")])],"isStart":false});
            extrude(context, id + "F17", {"entities" : qUnion([Q0, Q1, Q2]), "endBound" : BoundingType.UP_TO_SURFACE, "endBoundEntityFace" : qUnion([Q3]), "depth" : 25 * mm});
        }
    });
